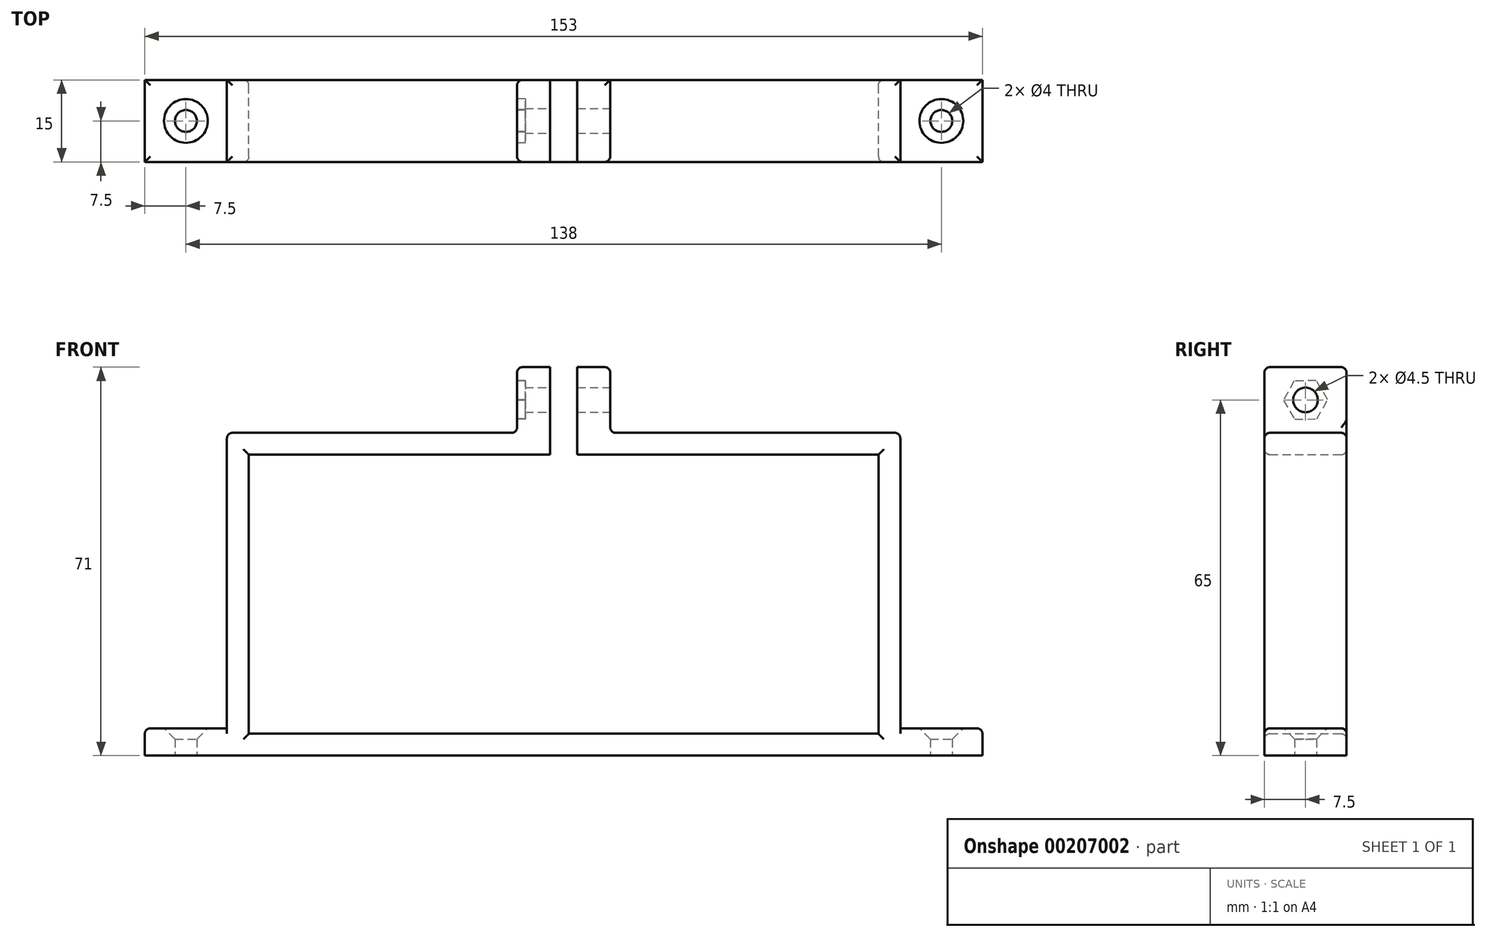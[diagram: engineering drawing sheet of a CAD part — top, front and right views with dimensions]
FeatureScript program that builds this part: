
annotation { "Feature Type Name" : "Feature", "Feature Type Description" : "" }
export const myFeature = defineFeature(function(context is Context, id is Id, definition is map)
    precondition{}
    {
        {
            var Q0;
            Q0=qCreatedBy(makeId("Front.planeOp"),FACE);
            var sketch = newSketch(context, id + "F0", { "sketchPlane" : qUnion([Q0])});
            skLineSegment(sketch, "E0.bottom", {"start": v(-57.5, 25.5) * mm, "end": v(-2.5, 25.5) * mm});
            skLineSegment(sketch, "E0.top", {"start": v(-57.5, -25.5) * mm, "end": v(57.5, -25.5) * mm});
            skLineSegment(sketch, "E0.left", {"start": v(-57.5, 25.5) * mm, "end": v(-57.5, -25.5) * mm});
            skLineSegment(sketch, "E0.right", {"start": v(57.5, 25.5) * mm, "end": v(57.5, -25.5) * mm});
            skLineSegment(sketch, "E1.bottom", {"start": v(-61.5, 29.5) * mm, "end": v(-8.5, 29.5) * mm});
            skLineSegment(sketch, "E1.top", {"start": v(-61.5, -29.5) * mm, "end": v(61.5, -29.5) * mm});
            skLineSegment(sketch, "E1.left", {"start": v(-61.5, 29.5) * mm, "end": v(-61.5, -29.5) * mm});
            skLineSegment(sketch, "E1.right", {"start": v(61.5, 29.5) * mm, "end": v(61.5, -29.5) * mm});
            skLineSegment(sketch, "E2.bottom", {"start": v(-2.5, 41.5) * mm, "end": v(-8.5, 41.5) * mm});
            skLineSegment(sketch, "E2.top", {"start": v(-2.5, 25.5) * mm, "end": v(-8.5, 25.5) * mm});
            skLineSegment(sketch, "E2.left", {"start": v(-2.5, 41.5) * mm, "end": v(-2.5, 25.5) * mm});
            skLineSegment(sketch, "E2.right", {"start": v(-8.5, 41.5) * mm, "end": v(-8.5, 29.5) * mm});
            skPoint(sketch, "E3.oppositeSnap0", {"position": v(-5.5, 41.5) * mm});
            skLineSegment(sketch, "E3.bottom", {"start": v(2.5, 25.5) * mm, "end": v(8.5, 25.5) * mm});
            skLineSegment(sketch, "E3.top", {"start": v(2.5, 41.5) * mm, "end": v(8.5, 41.5) * mm});
            skLineSegment(sketch, "E3.left", {"start": v(2.5, 25.5) * mm, "end": v(2.5, 41.5) * mm});
            skLineSegment(sketch, "E3.right", {"start": v(8.5, 29.5) * mm, "end": v(8.5, 41.5) * mm});
            skLineSegment(sketch, "E4.trimOffspring", {"start": v(8.5, 29.5) * mm, "end": v(61.5, 29.5) * mm});
            skLineSegment(sketch, "E5.trimOffspring", {"start": v(2.5, 25.5) * mm, "end": v(57.5, 25.5) * mm});
            skSolve(sketch);
        }
        {
            var Q0;
            Q0=makeQuery(id+"F0.imprint","IMPRINT",FACE,{"disambiguationData":[TD([[makeQuery(id+"F0.imprint","IMPRINT",EDGE,{"derivedFrom":sQuery(id+"F0.wireOp",EDGE,"E0.bottom")}),1.0]])]});
            extrude(context, id + "F1", {"entities" : qUnion([Q0]), "depth" : 15 * mm});
        }
        {
            var Q0;
            Q0=makeQuery(id+"F1.opExtrude","SWEPT_FACE",FACE,{"disambiguationData":[OSD([sQuery(id+"F0.wireOp",EDGE,"E3.right")])]});
            var sketch = newSketch(context, id + "F2", { "sketchPlane" : qUnion([Q0])});
            skCircle(sketch, "E6", {"center": v(-7.5, 35.5) * mm, "radius": 2.25 * mm});
            skPoint(sketch, "E6.centerSnap0", {"position": v(-15, 35.5) * mm});
            skPoint(sketch, "E6.centerSnap1", {"position": v(-7.5, 41.5) * mm});
            skSolve(sketch);
        }
        {
            var Q0;
            Q0=makeQuery(id+"F2.imprint","IMPRINT",FACE,{"disambiguationData":[TD([[makeQuery(id+"F2.imprint","IMPRINT",EDGE,{"derivedFrom":sQuery(id+"F2.wireOp",EDGE,"E6")}),1.0]])]});
            extrude(context, id + "F3", {"entities" : qUnion([Q0]), "operationType" : NewBodyOperationType.REMOVE, "oppositeDirection" : true, "depth" : 25 * mm});
        }
        {
            var Q0;
            Q0=makeQuery(id+"F1.opExtrude","SWEPT_FACE",FACE,{"disambiguationData":[OSD([sQuery(id+"F0.wireOp",EDGE,"E1.top")])]});
            var sketch = newSketch(context, id + "F4", { "sketchPlane" : qUnion([Q0])});
            skPoint(sketch, "E7.centerSnap0", {"position": v(-61.5, 7.5) * mm});
            skSolve(sketch);
        }
        {
            var Q0;
            Q0=makeQuery(id+"F1.opExtrude","SWEPT_FACE",FACE,{"disambiguationData":[OSD([sQuery(id+"F0.wireOp",EDGE,"E2.right")])]});
            var sketch = newSketch(context, id + "F5", { "sketchPlane" : qUnion([Q0])});
            skCircle(sketch, "E8.cCircle", {"center": v(7.5, 35.5) * mm, "radius": 3.5 * mm, "construction": true});
            skLineSegment(sketch, "E8.0", {"start": v(11.54, 35.43) * mm, "end": v(9.46, 31.96) * mm});
            skLineSegment(sketch, "E8.1", {"start": v(9.46, 31.96) * mm, "end": v(5.42, 32.04) * mm});
            skLineSegment(sketch, "E8.2", {"start": v(5.42, 32.04) * mm, "end": v(3.46, 35.57) * mm});
            skLineSegment(sketch, "E8.3", {"start": v(3.46, 35.57) * mm, "end": v(5.54, 39.04) * mm});
            skLineSegment(sketch, "E8.4", {"start": v(5.54, 39.04) * mm, "end": v(9.58, 38.96) * mm});
            skLineSegment(sketch, "E8.5", {"start": v(9.58, 38.96) * mm, "end": v(11.54, 35.43) * mm});
            skPoint(sketch, "E8.0.midPoint", {"position": v(10.5, 33.7) * mm});
            skSolve(sketch);
        }
        {
            var Q0;
            Q0=makeQuery(id+"F5.imprint","IMPRINT",FACE,{"disambiguationData":[TD([[makeQuery(id+"F5.imprint","IMPRINT",EDGE,{"derivedFrom":sQuery(id+"F5.wireOp",EDGE,"E8.0")}),-1.0]])]});
            extrude(context, id + "F6", {"entities" : qUnion([Q0]), "operationType" : NewBodyOperationType.REMOVE, "oppositeDirection" : true, "depth" : 1.5 * mm});
        }
        {
            var Q0;
            {var subQ0=sQuery(id+"F0.wireOp",EDGE,"E1.top");Q0=makeQuery(id+"F4.imprint","IMPRINT",FACE,{"disambiguationData":[TD([[makeQuery(id+"F4.imprint","IMPRINT",EDGE,{"derivedFrom":makeQuery(id+"F1.opExtrude","CAP_EDGE",EDGE,{"disambiguationData":[OSD([subQ0])],"isStart":true})}),1.0]])]});}
            var sketch = newSketch(context, id + "F7", { "sketchPlane" : qUnion([Q0])});
            skLineSegment(sketch, "E9.bottom", {"start": v(-61.5, 15) * mm, "end": v(-76.5, 15) * mm});
            skLineSegment(sketch, "E9.top", {"start": v(-61.5, 0) * mm, "end": v(-76.5, 0) * mm});
            skLineSegment(sketch, "E9.left", {"start": v(-61.5, 15) * mm, "end": v(-61.5, 0) * mm});
            skLineSegment(sketch, "E9.right", {"start": v(-76.5, 15) * mm, "end": v(-76.5, 0) * mm});
            skCircle(sketch, "E10", {"center": v(-69, 7.5) * mm, "radius": 2 * mm});
            skPoint(sketch, "E10.centerSnap0", {"position": v(-76.5, 7.5) * mm});
            skPoint(sketch, "E10.centerSnap1", {"position": v(-69, 15) * mm});
            skLineSegment(sketch, "E11.MirrorCS", {"start": v(61.5, 15) * mm, "end": v(76.5, 15) * mm});
            skLineSegment(sketch, "E12.MirrorCS", {"start": v(76.5, 15) * mm, "end": v(76.5, 0) * mm});
            skLineSegment(sketch, "E13.MirrorCS", {"start": v(61.5, 0) * mm, "end": v(76.5, 0) * mm});
            skLineSegment(sketch, "E14.MirrorCS", {"start": v(61.5, 15) * mm, "end": v(61.5, 0) * mm});
            skCircle(sketch, "E15.MirrorC", {"center": v(69, 7.5) * mm, "radius": 2 * mm});
            skSolve(sketch);
        }
        {
            var Q0;
            Q0=makeQuery(id+"F7.imprint","IMPRINT",FACE,{"disambiguationData":[TD([[makeQuery(id+"F7.imprint","IMPRINT",EDGE,{"derivedFrom":sQuery(id+"F7.wireOp",EDGE,"E9.bottom")}),1.0]])]});
            var Q1;
            Q1=makeQuery(id+"F7.imprint","IMPRINT",FACE,{"disambiguationData":[TD([[makeQuery(id+"F7.imprint","IMPRINT",EDGE,{"derivedFrom":sQuery(id+"F7.wireOp",EDGE,"E11.MirrorCS")}),-1.0]])]});
            extrude(context, id + "F8", {"entities" : qUnion([Q0, Q1]), "operationType" : NewBodyOperationType.ADD, "oppositeDirection" : true, "depth" : 5 * mm});
        }
        {
            var Q0;
            Q0=makeQuery(id+"F1.opExtrude","CAP_EDGE",EDGE,{"disambiguationData":[OSD([sQuery(id+"F0.wireOp",EDGE,"E5.trimOffspring")])],"isStart":true});
            var Q1;
            Q1=makeQuery(id+"F1.opExtrude","CAP_EDGE",EDGE,{"disambiguationData":[OSD([sQuery(id+"F0.wireOp",EDGE,"E0.right")])],"isStart":true});
            var Q2;
            Q2=makeQuery(id+"F1.opExtrude","CAP_EDGE",EDGE,{"disambiguationData":[OSD([sQuery(id+"F0.wireOp",EDGE,"E0.bottom"),sQuery(id+"F0.wireOp",EDGE,"E2.top")])],"isStart":true});
            var Q3;
            Q3=makeQuery(id+"F1.opExtrude","CAP_EDGE",EDGE,{"disambiguationData":[OSD([sQuery(id+"F0.wireOp",EDGE,"E0.left")])],"isStart":true});
            var Q4;
            Q4=makeQuery(id+"F1.opExtrude","CAP_EDGE",EDGE,{"disambiguationData":[OSD([sQuery(id+"F0.wireOp",EDGE,"E0.top")])],"isStart":true});
            var Q5;
            Q5=makeQuery(id+"F1.opExtrude","CAP_EDGE",EDGE,{"disambiguationData":[OSD([sQuery(id+"F0.wireOp",EDGE,"E0.bottom"),sQuery(id+"F0.wireOp",EDGE,"E2.top")])],"isStart":false});
            var Q6;
            Q6=makeQuery(id+"F1.opExtrude","CAP_EDGE",EDGE,{"disambiguationData":[OSD([sQuery(id+"F0.wireOp",EDGE,"E5.trimOffspring")])],"isStart":false});
            var Q7;
            Q7=makeQuery(id+"F1.opExtrude","CAP_EDGE",EDGE,{"disambiguationData":[OSD([sQuery(id+"F0.wireOp",EDGE,"E0.left")])],"isStart":false});
            var Q8;
            Q8=makeQuery(id+"F1.opExtrude","CAP_EDGE",EDGE,{"disambiguationData":[OSD([sQuery(id+"F0.wireOp",EDGE,"E0.top")])],"isStart":false});
            var Q9;
            Q9=makeQuery(id+"F1.opExtrude","CAP_EDGE",EDGE,{"disambiguationData":[OSD([sQuery(id+"F0.wireOp",EDGE,"E0.right")])],"isStart":false});
            var Q10;
            Q10=makeQuery(id+"F8.opExtrude","CAP_EDGE",EDGE,{"disambiguationData":[OSD([sQuery(id+"F7.wireOp",EDGE,"E9.bottom")])],"isStart":false});
            var Q11;
            Q11=makeQuery(id+"F8.opExtrude","CAP_EDGE",EDGE,{"disambiguationData":[OSD([sQuery(id+"F7.wireOp",EDGE,"E9.right")])],"isStart":false});
            var Q12;
            Q12=makeQuery(id+"F8.opExtrude","CAP_EDGE",EDGE,{"disambiguationData":[OSD([sQuery(id+"F7.wireOp",EDGE,"E9.top")])],"isStart":false});
            var Q13;
            Q13=makeQuery(id+"F8.opExtrude","CAP_EDGE",EDGE,{"disambiguationData":[OSD([sQuery(id+"F7.wireOp",EDGE,"E13.MirrorCS")])],"isStart":false});
            var Q14;
            Q14=makeQuery(id+"F8.opExtrude","CAP_EDGE",EDGE,{"disambiguationData":[OSD([sQuery(id+"F7.wireOp",EDGE,"E12.MirrorCS")])],"isStart":false});
            var Q15;
            Q15=makeQuery(id+"F8.opExtrude","CAP_EDGE",EDGE,{"disambiguationData":[OSD([sQuery(id+"F7.wireOp",EDGE,"E11.MirrorCS")])],"isStart":false});
            var Q16;
            Q16=makeQuery(id+"F8.opExtrude","CAP_EDGE",EDGE,{"disambiguationData":[OSD([sQuery(id+"F7.wireOp",EDGE,"E14.MirrorCS")])],"isStart":false});
            var Q17;
            Q17=makeQuery(id+"F8.opExtrude","CAP_EDGE",EDGE,{"disambiguationData":[OSD([sQuery(id+"F7.wireOp",EDGE,"E9.left")])],"isStart":false});
            var Q18;
            Q18=makeQuery(id+"F1.opExtrude","CAP_EDGE",EDGE,{"disambiguationData":[OSD([sQuery(id+"F0.wireOp",EDGE,"E1.bottom")])],"isStart":false});
            var Q19;
            Q19=makeQuery(id+"F1.opExtrude","CAP_EDGE",EDGE,{"disambiguationData":[OSD([sQuery(id+"F0.wireOp",EDGE,"E1.bottom")])],"isStart":true});
            var Q20;
            Q20=makeQuery(id+"F1.opExtrude","CAP_EDGE",EDGE,{"disambiguationData":[OSD([sQuery(id+"F0.wireOp",EDGE,"E4.trimOffspring")])],"isStart":true});
            var Q21;
            Q21=makeQuery(id+"F1.opExtrude","SWEPT_EDGE",EDGE,{"disambiguationData":[OSD([sQuery(id+"F0.wireOp",EDGE,"E3.right"),sQuery(id+"F0.wireOp",EDGE,"E4.trimOffspring")])]});
            var Q22;
            Q22=makeQuery(id+"F1.opExtrude","SWEPT_EDGE",EDGE,{"disambiguationData":[OSD([sQuery(id+"F0.wireOp",EDGE,"E1.bottom"),sQuery(id+"F0.wireOp",EDGE,"E2.right")])]});
            var Q23;
            Q23=makeQuery(id+"F6.boolean.opBoolean","COPY",EDGE,{"derivedFrom":makeQuery(id+"F6.opExtrude","CAP_EDGE",EDGE,{"disambiguationData":[OSD([sQuery(id+"F5.wireOp",EDGE,"E8.3")])],"isStart":true})});
            var Q24;
            Q24=makeQuery(id+"F1.opExtrude","CAP_EDGE",EDGE,{"disambiguationData":[OSD([sQuery(id+"F0.wireOp",EDGE,"E2.right")])],"isStart":false});
            var Q25;
            Q25=makeQuery(id+"F1.opExtrude","CAP_EDGE",EDGE,{"disambiguationData":[OSD([sQuery(id+"F0.wireOp",EDGE,"E2.right")])],"isStart":true});
            var Q26;
            Q26=makeQuery(id+"F1.opExtrude","SWEPT_EDGE",EDGE,{"disambiguationData":[OSD([sQuery(id+"F0.wireOp",EDGE,"E2.bottom"),sQuery(id+"F0.wireOp",EDGE,"E2.right")])]});
            var Q27;
            Q27=makeQuery(id+"F1.opExtrude","SWEPT_EDGE",EDGE,{"disambiguationData":[OSD([sQuery(id+"F0.wireOp",EDGE,"E3.top"),sQuery(id+"F0.wireOp",EDGE,"E3.right")])]});
            var Q28;
            Q28=makeQuery(id+"F1.opExtrude","CAP_EDGE",EDGE,{"disambiguationData":[OSD([sQuery(id+"F0.wireOp",EDGE,"E3.right")])],"isStart":false});
            var Q29;
            Q29=makeQuery(id+"F1.opExtrude","CAP_EDGE",EDGE,{"disambiguationData":[OSD([sQuery(id+"F0.wireOp",EDGE,"E4.trimOffspring")])],"isStart":false});
            var Q30;
            Q30=makeQuery(id+"F1.opExtrude","SWEPT_EDGE",EDGE,{"disambiguationData":[OSD([sQuery(id+"F0.wireOp",EDGE,"E1.right"),sQuery(id+"F0.wireOp",EDGE,"E4.trimOffspring")])]});
            var Q31;
            Q31=makeQuery(id+"F1.opExtrude","SWEPT_EDGE",EDGE,{"disambiguationData":[OSD([sQuery(id+"F0.wireOp",EDGE,"E1.bottom"),sQuery(id+"F0.wireOp",EDGE,"E1.left")])]});
            var Q32;
            Q32=makeQuery(id+"F1.opExtrude","CAP_EDGE",EDGE,{"disambiguationData":[OSD([sQuery(id+"F0.wireOp",EDGE,"E3.top")])],"isStart":true});
            var Q33;
            Q33=makeQuery(id+"F1.opExtrude","CAP_EDGE",EDGE,{"disambiguationData":[OSD([sQuery(id+"F0.wireOp",EDGE,"E2.bottom")])],"isStart":true});
            var Q34;
            Q34=makeQuery(id+"F1.opExtrude","CAP_EDGE",EDGE,{"disambiguationData":[OSD([sQuery(id+"F0.wireOp",EDGE,"E2.bottom")])],"isStart":false});
            var Q35;
            Q35=makeQuery(id+"F1.opExtrude","CAP_EDGE",EDGE,{"disambiguationData":[OSD([sQuery(id+"F0.wireOp",EDGE,"E3.top")])],"isStart":false});
            fillet(context, id + "F9", {"entities" : qUnion([Q0, Q1, Q2, Q3, Q4, Q5, Q6, Q7, Q8, Q9, Q10, Q11, Q12, Q13, Q14, Q15, Q16, Q17, Q18, Q19, Q20, Q21, Q22, Q23, Q24, Q25, Q26, Q27, Q28, Q29, Q30, Q31, Q32, Q33, Q34, Q35]), "radius" : 1 * mm, "tangentPropagation" : true, "allowEdgeOverflow" : false});
        }
        {
            var Q0;
            Q0=makeQuery(id+"F8.opExtrude","CAP_EDGE",EDGE,{"disambiguationData":[OSD([sQuery(id+"F7.wireOp",EDGE,"E15.MirrorC")])],"isStart":false});
            var Q1;
            Q1=makeQuery(id+"F8.opExtrude","CAP_EDGE",EDGE,{"disambiguationData":[OSD([sQuery(id+"F7.wireOp",EDGE,"E10")])],"isStart":false});
            chamfer(context, id + "F10", {"entities" : qUnion([Q0, Q1]), "width" : 2 * mm, "tangentPropagation" : true});
        }
    });
